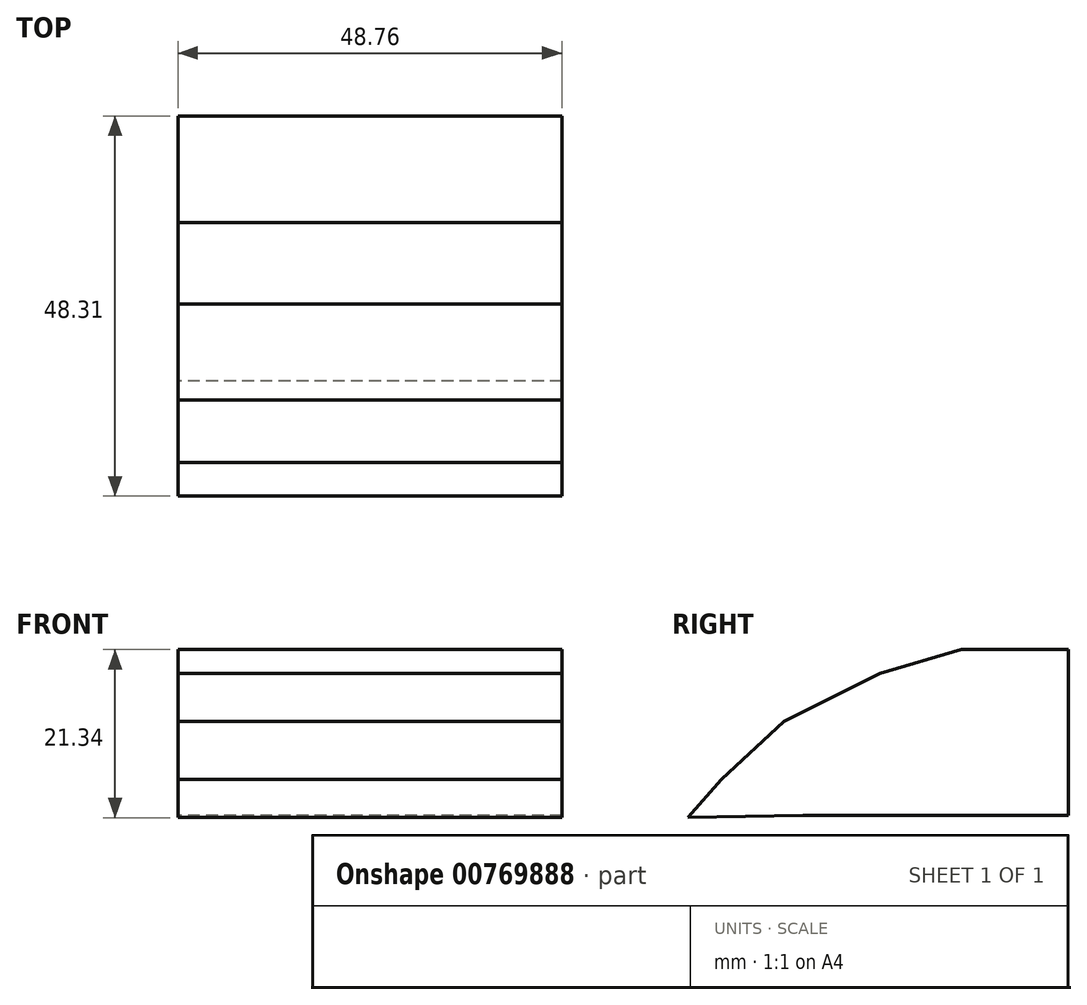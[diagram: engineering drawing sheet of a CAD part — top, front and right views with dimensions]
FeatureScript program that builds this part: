
annotation { "Feature Type Name" : "Feature", "Feature Type Description" : "" }
export const myFeature = defineFeature(function(context is Context, id is Id, definition is map)
    precondition{}
    {
        {
            var Q0;
            Q0=qCreatedBy(makeId("Right.planeOp"),FACE);
            var sketch = newSketch(context, id + "F0", { "sketchPlane" : qUnion([Q0])});
            skLineSegment(sketch, "E0", {"start": v(-33.68, -51.51) * mm, "end": v(0, -51.51) * mm});
            skLineSegment(sketch, "E1", {"start": v(0, -51.51) * mm, "end": v(0, -30.48) * mm});
            skLineSegment(sketch, "E2", {"start": v(0, -30.48) * mm, "end": v(-13.56, -30.48) * mm});
            skLineSegment(sketch, "E3", {"start": v(-13.56, -30.48) * mm, "end": v(-23.93, -33.53) * mm});
            skLineSegment(sketch, "E4", {"start": v(-23.93, -33.53) * mm, "end": v(-36.12, -39.62) * mm});
            skLineSegment(sketch, "E5", {"start": v(-36.12, -39.62) * mm, "end": v(-44.04, -46.94) * mm});
            skLineSegment(sketch, "E6", {"start": v(-44.04, -46.94) * mm, "end": v(-48.31, -51.82) * mm});
            skLineSegment(sketch, "E7", {"start": v(-48.31, -51.82) * mm, "end": v(-33.68, -51.51) * mm});
            skSolve(sketch);
        }
        {
            var Q0;
            Q0 = qSketchRegion(id + "F0", true);
            extrude(context, id + "F1", {"entities" : qUnion([Q0]), "endBound" : BoundingType.SYMMETRIC, "depth" : 48.77 * mm, "offsetDistance" : 25.4 * mm});
        }
    });
